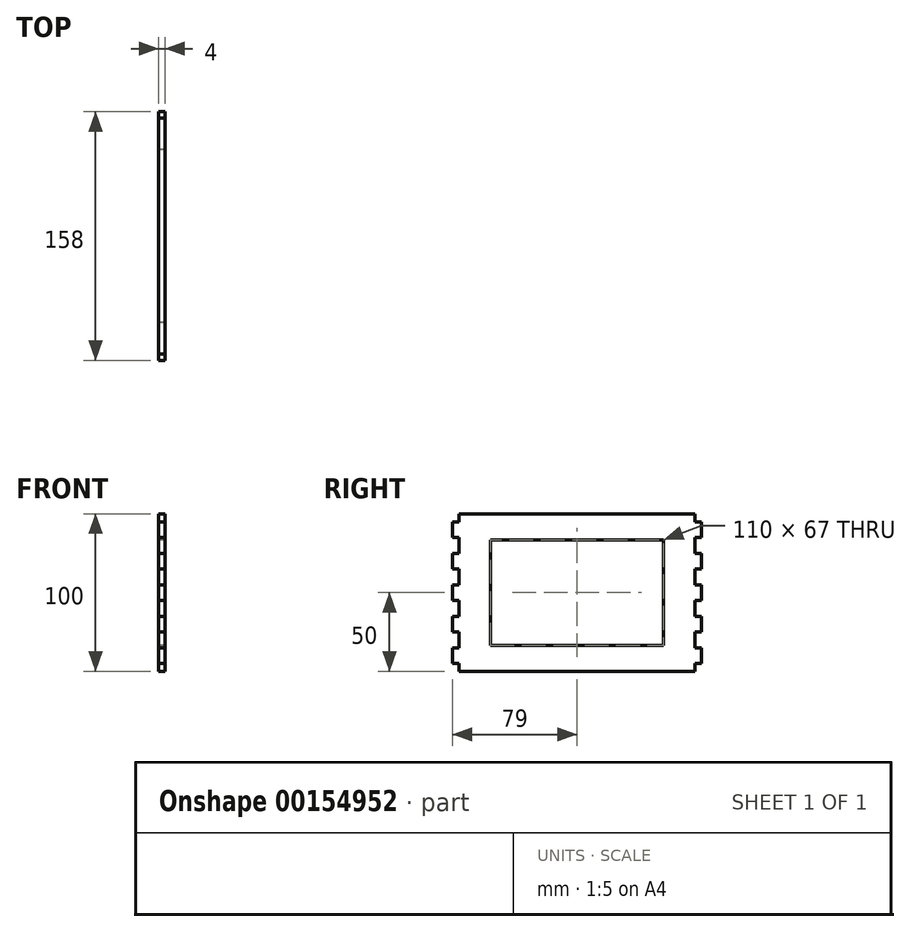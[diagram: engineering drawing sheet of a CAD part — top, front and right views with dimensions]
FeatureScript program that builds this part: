
annotation { "Feature Type Name" : "Feature", "Feature Type Description" : "" }
export const myFeature = defineFeature(function(context is Context, id is Id, definition is map)
    precondition{}
    {
        {
            var Q0;
            Q0=qCreatedBy(makeId("Right.planeOp"),FACE);
            var sketch = newSketch(context, id + "F0", { "sketchPlane" : qUnion([Q0])});
            skLineSegment(sketch, "E0.bottom", {"start": v(75, 50) * mm, "end": v(-75, 50) * mm});
            skLineSegment(sketch, "E0.top", {"start": v(75, -50) * mm, "end": v(-75, -50) * mm});
            skLineSegment(sketch, "E0.left", {"start": v(75, 50) * mm, "end": v(75, -50) * mm});
            skLineSegment(sketch, "E0.right", {"start": v(-75, 50) * mm, "end": v(-75, -50) * mm});
            skPoint(sketch, "E0.middle", {"position": v(0, 0) * mm});
            skLineSegment(sketch, "E1.bottom", {"start": v(55, 33.5) * mm, "end": v(-55, 33.5) * mm});
            skLineSegment(sketch, "E1.top", {"start": v(55, -33.5) * mm, "end": v(-55, -33.5) * mm});
            skLineSegment(sketch, "E1.left", {"start": v(55, 33.5) * mm, "end": v(55, -33.5) * mm});
            skLineSegment(sketch, "E1.right", {"start": v(-55, 33.5) * mm, "end": v(-55, -33.5) * mm});
            skSolve(sketch);
        }
        {
            var Q0;
            Q0 = qSketchRegion(id + "F0", true);
            extrude(context, id + "F1", {"entities" : qUnion([Q0]), "depth" : 4 * mm});
        }
        {
            var Q0;
            Q0=makeQuery(id+"F1.opExtrude","CAP_FACE",FACE,{"disambiguationData":[OSD([sQuery(id+"F0.wireOp",EDGE,"E0.bottom"),sQuery(id+"F0.wireOp",EDGE,"E0.top"),sQuery(id+"F0.wireOp",EDGE,"E0.left"),sQuery(id+"F0.wireOp",EDGE,"E0.right"),sQuery(id+"F0.wireOp",EDGE,"E1.bottom"),sQuery(id+"F0.wireOp",EDGE,"E1.top"),sQuery(id+"F0.wireOp",EDGE,"E1.left"),sQuery(id+"F0.wireOp",EDGE,"E1.right")])],"isStart":false});
            var sketch = newSketch(context, id + "F2", { "sketchPlane" : qUnion([Q0])});
            skLineSegment(sketch, "E2", {"start": v(-75, 0) * mm, "end": v(-79, 0) * mm});
            skPoint(sketch, "E2.endSnap0", {"position": v(-75, 0) * mm});
            skLineSegment(sketch, "E3", {"start": v(-79, 0) * mm, "end": v(-79, 5) * mm});
            skLineSegment(sketch, "E4", {"start": v(-79, 5) * mm, "end": v(-75, 5) * mm});
            skLineSegment(sketch, "E5", {"start": v(-75, 5) * mm, "end": v(-75, -5) * mm});
            skLineSegment(sketch, "E6", {"start": v(-75, -5) * mm, "end": v(-79, -5) * mm});
            skLineSegment(sketch, "E7", {"start": v(-79, -5) * mm, "end": v(-79, 0) * mm});
            skLineSegment(sketch, "E8.0.1.0", {"start": v(-79, 25) * mm, "end": v(-75, 25) * mm});
            skLineSegment(sketch, "E8.0.1.1", {"start": v(-79, 20) * mm, "end": v(-79, 25) * mm});
            skLineSegment(sketch, "E8.0.1.2", {"start": v(-75, 25) * mm, "end": v(-75, 15) * mm});
            skLineSegment(sketch, "E8.0.1.3", {"start": v(-79, 15) * mm, "end": v(-79, 20) * mm});
            skLineSegment(sketch, "E8.0.1.4", {"start": v(-75, 15) * mm, "end": v(-79, 15) * mm});
            skLineSegment(sketch, "E8.0.2.0", {"start": v(-79, 45) * mm, "end": v(-75, 45) * mm});
            skLineSegment(sketch, "E8.0.2.1", {"start": v(-79, 40) * mm, "end": v(-79, 45) * mm});
            skLineSegment(sketch, "E8.0.2.2", {"start": v(-75, 45) * mm, "end": v(-75, 35) * mm});
            skLineSegment(sketch, "E8.0.2.3", {"start": v(-79, 35) * mm, "end": v(-79, 40) * mm});
            skLineSegment(sketch, "E8.0.2.4", {"start": v(-75, 35) * mm, "end": v(-79, 35) * mm});
            skLineSegment(sketch, "E8.direction1", {"start": v(-79, 5) * mm, "end": v(-54, 5) * mm, "construction": true});
            skLineSegment(sketch, "E8.direction2", {"start": v(-79, 5) * mm, "end": v(-79, 25) * mm, "construction": true});
            skLineSegment(sketch, "E9.MirrorCS", {"start": v(-75, -45) * mm, "end": v(-75, -35) * mm});
            skLineSegment(sketch, "E10.MirrorCS", {"start": v(-79, -40) * mm, "end": v(-79, -45) * mm});
            skLineSegment(sketch, "E11.MirrorCS", {"start": v(-79, -35) * mm, "end": v(-79, -40) * mm});
            skLineSegment(sketch, "E12.MirrorCS", {"start": v(-79, -45) * mm, "end": v(-75, -45) * mm});
            skLineSegment(sketch, "E13.MirrorCS", {"start": v(-75, -35) * mm, "end": v(-79, -35) * mm});
            skLineSegment(sketch, "E14.MirrorCS", {"start": v(-79, -25) * mm, "end": v(-75, -25) * mm});
            skLineSegment(sketch, "E15.MirrorCS", {"start": v(-79, -5) * mm, "end": v(-79, -25) * mm, "construction": true});
            skLineSegment(sketch, "E16.MirrorCS", {"start": v(-75, -25) * mm, "end": v(-75, -15) * mm});
            skLineSegment(sketch, "E17.MirrorCS", {"start": v(-75, -15) * mm, "end": v(-79, -15) * mm});
            skLineSegment(sketch, "E18", {"start": v(-79, -15) * mm, "end": v(-79, -25) * mm});
            skLineSegment(sketch, "E19", {"start": v(0, 50) * mm, "end": v(0, 45.57) * mm});
            skPoint(sketch, "E19.endSnap0", {"position": v(0, 50) * mm});
            skLineSegment(sketch, "E20.MirrorCS", {"start": v(79, -15) * mm, "end": v(79, -25) * mm});
            skLineSegment(sketch, "E21.MirrorCS", {"start": v(79, 20) * mm, "end": v(79, 25) * mm});
            skLineSegment(sketch, "E22.MirrorCS", {"start": v(79, 15) * mm, "end": v(79, 20) * mm});
            skLineSegment(sketch, "E23.MirrorCS", {"start": v(79, -25) * mm, "end": v(75, -25) * mm});
            skLineSegment(sketch, "E24.MirrorCS", {"start": v(79, 25) * mm, "end": v(75, 25) * mm});
            skLineSegment(sketch, "E25.MirrorCS", {"start": v(79, -5) * mm, "end": v(79, 0) * mm});
            skLineSegment(sketch, "E26.MirrorCS", {"start": v(75, -5) * mm, "end": v(79, -5) * mm});
            skLineSegment(sketch, "E27.MirrorCS", {"start": v(75, 25) * mm, "end": v(75, 15) * mm});
            skLineSegment(sketch, "E28.MirrorCS", {"start": v(75, 5) * mm, "end": v(75, -5) * mm});
            skLineSegment(sketch, "E29.MirrorCS", {"start": v(79, 5) * mm, "end": v(75, 5) * mm});
            skLineSegment(sketch, "E30.MirrorCS", {"start": v(79, 0) * mm, "end": v(79, 5) * mm});
            skLineSegment(sketch, "E31.MirrorCS", {"start": v(75, 0) * mm, "end": v(79, 0) * mm});
            skLineSegment(sketch, "E32.MirrorCS", {"start": v(75, 15) * mm, "end": v(79, 15) * mm});
            skLineSegment(sketch, "E33.MirrorCS", {"start": v(75, 35) * mm, "end": v(79, 35) * mm});
            skLineSegment(sketch, "E34.MirrorCS", {"start": v(79, 45) * mm, "end": v(75, 45) * mm});
            skLineSegment(sketch, "E35.MirrorCS", {"start": v(75, -25) * mm, "end": v(75, -15) * mm});
            skLineSegment(sketch, "E36.MirrorCS", {"start": v(79, 40) * mm, "end": v(79, 45) * mm});
            skLineSegment(sketch, "E37.MirrorCS", {"start": v(79, -35) * mm, "end": v(79, -40) * mm});
            skLineSegment(sketch, "E38.MirrorCS", {"start": v(75, -35) * mm, "end": v(79, -35) * mm});
            skLineSegment(sketch, "E39.MirrorCS", {"start": v(75, -45) * mm, "end": v(75, -35) * mm});
            skLineSegment(sketch, "E40.MirrorCS", {"start": v(79, -5) * mm, "end": v(79, -25) * mm, "construction": true});
            skLineSegment(sketch, "E41.MirrorCS", {"start": v(79, -45) * mm, "end": v(75, -45) * mm});
            skLineSegment(sketch, "E42.MirrorCS", {"start": v(79, 35) * mm, "end": v(79, 40) * mm});
            skLineSegment(sketch, "E43.MirrorCS", {"start": v(75, 45) * mm, "end": v(75, 35) * mm});
            skPoint(sketch, "E44.MirrorP", {"position": v(75, 0) * mm});
            skLineSegment(sketch, "E45.MirrorCS", {"start": v(75, -15) * mm, "end": v(79, -15) * mm});
            skLineSegment(sketch, "E46.MirrorCS", {"start": v(79, 5) * mm, "end": v(79, 25) * mm, "construction": true});
            skLineSegment(sketch, "E47.MirrorCS", {"start": v(79, -40) * mm, "end": v(79, -45) * mm});
            skSolve(sketch);
        }
        {
            var Q0;
            Q0 = qSketchRegion(id + "F2", true);
            extrude(context, id + "F3", {"entities" : qUnion([Q0]), "operationType" : NewBodyOperationType.ADD, "oppositeDirection" : true, "depth" : 4 * mm});
        }
    });
